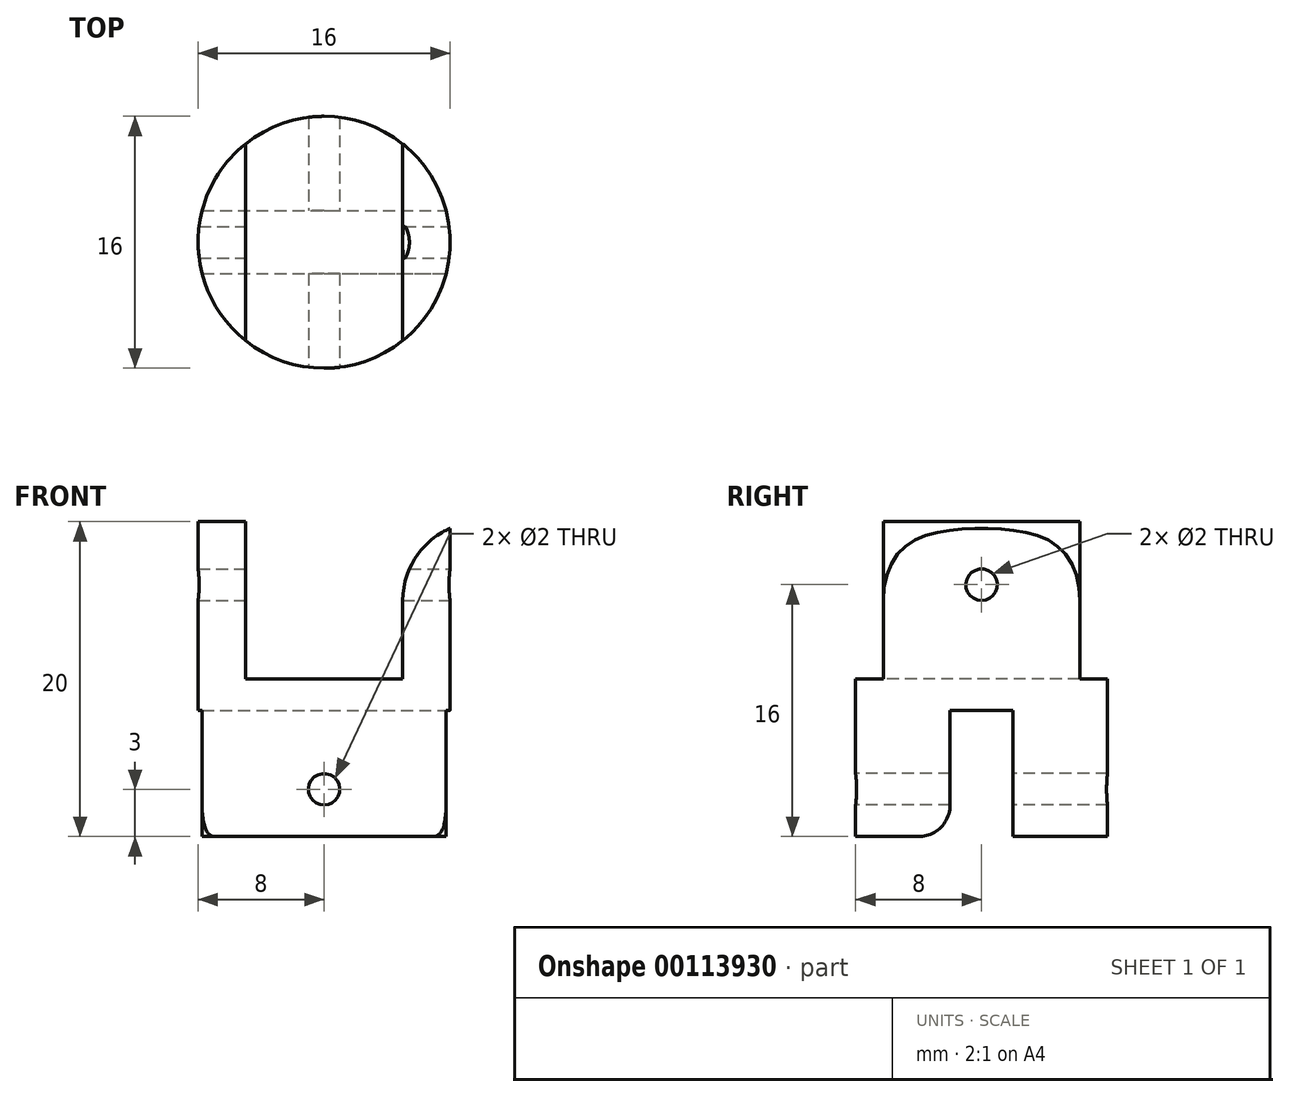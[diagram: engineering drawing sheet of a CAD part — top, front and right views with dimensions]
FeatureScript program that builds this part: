
annotation { "Feature Type Name" : "Feature", "Feature Type Description" : "" }
export const myFeature = defineFeature(function(context is Context, id is Id, definition is map)
    precondition{}
    {
        {
            var Q0;
            Q0=qCreatedBy(makeId("Top.planeOp"),FACE);
            var sketch = newSketch(context, id + "F0", { "sketchPlane" : qUnion([Q0])});
            skCircle(sketch, "E0", {"center": v(0, 0) * mm, "radius": 8 * mm});
            skSolve(sketch);
        }
        {
            var Q0;
            Q0=makeQuery(id+"F0.imprint","IMPRINT",FACE,{"disambiguationData":[TD([[makeQuery(id+"F0.imprint","IMPRINT",EDGE,{"derivedFrom":sQuery(id+"F0.wireOp",EDGE,"E0")}),1.0]])]});
            extrude(context, id + "F1", {"entities" : qUnion([Q0]), "endBound" : BoundingType.SYMMETRIC, "depth" : 20 * mm});
        }
        {
            var Q0;
            Q0=makeQuery(id+"F1.opExtrude","CAP_FACE",FACE,{"disambiguationData":[OSD([sQuery(id+"F0.wireOp",EDGE,"E0")])],"isStart":false});
            var sketch = newSketch(context, id + "F2", { "sketchPlane" : qUnion([Q0])});
            skLineSegment(sketch, "E1.bottom", {"start": v(-5, 12.58) * mm, "end": v(5, 12.58) * mm});
            skLineSegment(sketch, "E1.top", {"start": v(-5, -12.58) * mm, "end": v(5, -12.58) * mm});
            skLineSegment(sketch, "E1.left", {"start": v(-5, 12.58) * mm, "end": v(-5, -12.58) * mm});
            skLineSegment(sketch, "E1.right", {"start": v(5, 12.58) * mm, "end": v(5, -12.58) * mm});
            skPoint(sketch, "E1.middle", {"position": v(0, 0) * mm});
            skSolve(sketch);
        }
        {
            var Q0;
            {var subQ0=sQuery(id+"F2.wireOp",EDGE,"E1.left");var subQ1=makeQuery(id+"F1.opExtrude","CAP_EDGE",EDGE,{"disambiguationData":[OSD([sQuery(id+"F0.wireOp",EDGE,"E0")])],"isStart":false});var subQ2=makeQuery(id+"F2.imprint","INTERSECT",VERTEX,{"disambiguationData":[OD(0.0)],"derivedFrom":[subQ1,subQ0]});Q0=makeQuery(id+"F2.imprint","IMPRINT",FACE,{"disambiguationData":[TD([[makeQuery(id+"F2.imprint","IMPRINT",EDGE,{"disambiguationData":[TD([[subQ2,-1.0]])],"derivedFrom":subQ0}),1.0]])]});}
            extrude(context, id + "F3", {"entities" : qUnion([Q0]), "operationType" : NewBodyOperationType.REMOVE, "oppositeDirection" : true, "depth" : 10 * mm});
        }
        {
            var Q0;
            Q0=makeQuery(id+"F1.opExtrude","CAP_FACE",FACE,{"disambiguationData":[OSD([sQuery(id+"F0.wireOp",EDGE,"E0")])],"isStart":true});
            var sketch = newSketch(context, id + "F4", { "sketchPlane" : qUnion([Q0])});
            skLineSegment(sketch, "E2.bottom", {"start": v(-10, 2) * mm, "end": v(10, 2) * mm});
            skLineSegment(sketch, "E2.top", {"start": v(-10, -2) * mm, "end": v(10, -2) * mm});
            skLineSegment(sketch, "E2.left", {"start": v(-10, 2) * mm, "end": v(-10, -2) * mm});
            skLineSegment(sketch, "E2.right", {"start": v(10, 2) * mm, "end": v(10, -2) * mm});
            skPoint(sketch, "E2.middle", {"position": v(0, 0) * mm});
            skSolve(sketch);
        }
        {
            var Q0;
            {var subQ0=sQuery(id+"F4.wireOp",EDGE,"E2.bottom");var subQ1=makeQuery(id+"F1.opExtrude","CAP_EDGE",EDGE,{"disambiguationData":[OSD([sQuery(id+"F0.wireOp",EDGE,"E0")])],"isStart":true});var subQ2=makeQuery(id+"F4.imprint","INTERSECT",VERTEX,{"disambiguationData":[OD(0.0)],"derivedFrom":[subQ1,subQ0]});Q0=makeQuery(id+"F4.imprint","IMPRINT",FACE,{"disambiguationData":[TD([[makeQuery(id+"F4.imprint","IMPRINT",EDGE,{"disambiguationData":[TD([[subQ2,-1.0]])],"derivedFrom":subQ0}),-1.0]])]});}
            extrude(context, id + "F5", {"entities" : qUnion([Q0]), "operationType" : NewBodyOperationType.REMOVE, "oppositeDirection" : true, "depth" : 8 * mm});
        }
        {
            var Q0;
            Q0=makeQuery(id+"F5.boolean.opBoolean","COPY",EDGE,{"derivedFrom":makeQuery(id+"F5.opExtrude","CAP_EDGE",EDGE,{"disambiguationData":[OSD([sQuery(id+"F4.wireOp",EDGE,"E2.top")])],"isStart":true})});
            var Q1;
            Q1=makeQuery(id+"F5.boolean.opBoolean","COPY",EDGE,{"derivedFrom":makeQuery(id+"F5.opExtrude","CAP_EDGE",EDGE,{"disambiguationData":[OSD([sQuery(id+"F4.wireOp",EDGE,"E2.bottom")])],"isStart":true})});
            fillet(context, id + "F6", {"entities" : qUnion([Q0, Q1]), "radius" : 2 * mm, "tangentPropagation" : true, "allowEdgeOverflow" : false});
        }
        {
            var Q0;
            Q0=makeQuery(id+"F3.boolean.opBoolean","COPY",EDGE,{"derivedFrom":makeQuery(id+"F3.opExtrude","CAP_EDGE",EDGE,{"disambiguationData":[OSD([sQuery(id+"F2.wireOp",EDGE,"E1.left")])],"isStart":true})});
            var Q1;
            Q1=makeQuery(id+"F3.boolean.opBoolean","COPY",EDGE,{"derivedFrom":makeQuery(id+"F3.opExtrude","CAP_EDGE",EDGE,{"disambiguationData":[OSD([sQuery(id+"F2.wireOp",EDGE,"E1.right")])],"isStart":true})});
            fillet(context, id + "F7", {"entities" : qUnion([Q0, Q1]), "radius" : 5 * mm, "tangentPropagation" : true, "allowEdgeOverflow" : false});
        }
        {
            var Q0;
            Q0=qCreatedBy(makeId("Right.planeOp"),FACE);
            var sketch = newSketch(context, id + "F8", { "sketchPlane" : qUnion([Q0])});
            skLineSegment(sketch, "E3", {"start": v(0, 0) * mm, "end": v(0, 6) * mm});
            skCircle(sketch, "E4", {"center": v(0, 6) * mm, "radius": 1 * mm});
            skSolve(sketch);
        }
        {
            var Q0;
            Q0 = qSketchRegion(id + "F8", true);
            extrude(context, id + "F9", {"entities" : qUnion([Q0]), "operationType" : NewBodyOperationType.REMOVE, "endBound" : BoundingType.SYMMETRIC, "oppositeDirection" : true, "depth" : 25 * mm});
        }
        {
            var Q0;
            Q0=qCreatedBy(makeId("Front.planeOp"),FACE);
            var sketch = newSketch(context, id + "F10", { "sketchPlane" : qUnion([Q0])});
            skLineSegment(sketch, "E5", {"start": v(0, 0) * mm, "end": v(0, -7) * mm});
            skCircle(sketch, "E6", {"center": v(0, -7) * mm, "radius": 1 * mm});
            skSolve(sketch);
        }
        {
            var Q0;
            Q0 = qSketchRegion(id + "F10", true);
            extrude(context, id + "F11", {"entities" : qUnion([Q0]), "operationType" : NewBodyOperationType.REMOVE, "endBound" : BoundingType.SYMMETRIC, "oppositeDirection" : true, "depth" : 25 * mm});
        }
    });
